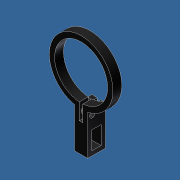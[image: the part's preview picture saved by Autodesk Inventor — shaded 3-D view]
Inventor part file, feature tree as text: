
AUTODESK INVENTOR PART (.ipt)
format: ipt  version: unknown  size: 232,960 bytes
history: native  units: in
note: dims shown in document units (in); Inventor stores cm internally (conversion verified against a paired STEP export)
features: sketch x5, extrude x4, hole x1, fillet x1
ambient origin geometry x8: Origin, YZ Plane, XZ Plane, XY Plane, X Axis, Y Axis, Z Axis, Center Point
bodies: Solid1 (feature_tree)
feature tree (11):
  extrude  "Extrusion1"  Depth=0.15in
  extrude  "Extrusion2"  Depth=0.1875in
  extrude  "Extrusion3"  Depth=2.0in
  hole  "Hole1"  [1 undecoded]
  fillet  "Fillet1"  Radius=0.05in
  extrude  "Extrusion4"  Depth=0.25in TaperAngle=0.0deg
  sketch  "Sketch1"  dims[d0=1.49in d1=0.15in]
  sketch  "Sketch2"  dims[d2=0.25in d3=0.0in d4=0.1875in]
  sketch  "Sketch3"  dims[d5=0.1875in d6=2.0in]
  sketch  "Sketch4"  dims[d7=0.5in d8=0.0in d9=0.05in d10=0.05in]
  sketch  "Sketch5"  dims[d11=1.2in d12=0.25in d13=0.0in d14=0.125in d15=0.125in d16=0.15in d17=0.75in d18=0.279in d19=0.25in d20=0.5635in d21=1.0in d22=0.8108in d23=0.125in d24=0.51in d25=0.115in d26=0.26in d27=0.1275in d28=0.25in d29=0.0in]
note: 1 required parameter value undecoded (feature->parameter linkage not recoverable at this tier; creation-order binding heuristic only, values carry confidence <= 0.55)
